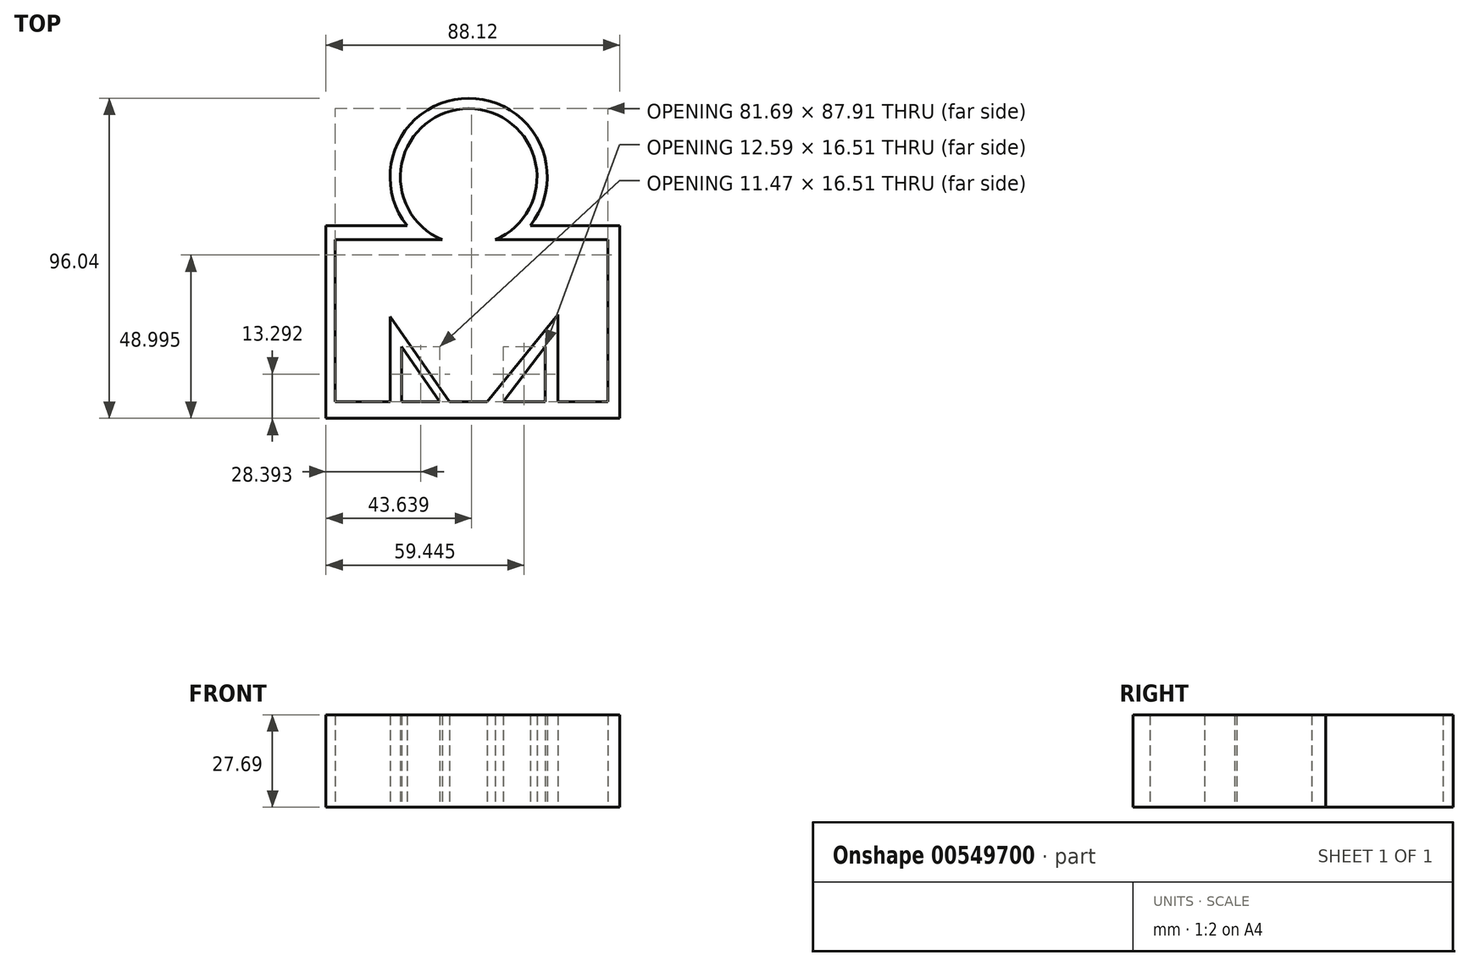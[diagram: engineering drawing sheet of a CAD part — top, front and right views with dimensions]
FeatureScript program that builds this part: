
annotation { "Feature Type Name" : "Feature", "Feature Type Description" : "" }
export const myFeature = defineFeature(function(context is Context, id is Id, definition is map)
    precondition{}
    {
        {
            var Q0;
            Q0=qCreatedBy(makeId("Top.planeOp"),FACE);
            var sketch = newSketch(context, id + "F0", { "sketchPlane" : qUnion([Q0])});
            skCircle(sketch, "E0", {"center": v(0, 0) * mm, "radius": 20.5 * mm});
            skLineSegment(sketch, "E1", {"start": v(-7.98, -18.87) * mm, "end": v(-40, -18.87) * mm});
            skLineSegment(sketch, "E2", {"start": v(-40, -18.87) * mm, "end": v(-40, -67.42) * mm});
            skLineSegment(sketch, "E3", {"start": v(-40, -67.42) * mm, "end": v(41.68, -67.42) * mm});
            skLineSegment(sketch, "E4", {"start": v(41.68, -67.42) * mm, "end": v(41.68, -18.87) * mm});
            skLineSegment(sketch, "E5", {"start": v(41.68, -18.87) * mm, "end": v(7.98, -18.87) * mm});
            skLineSegment(sketch, "E6", {"start": v(-20.14, -67.42) * mm, "end": v(-20.14, -50.92) * mm});
            skLineSegment(sketch, "E7", {"start": v(22.94, -67.42) * mm, "end": v(22.94, -50.92) * mm});
            skLineSegment(sketch, "E8", {"start": v(-20.14, -50.92) * mm, "end": v(-8.67, -67.42) * mm});
            skLineSegment(sketch, "E9", {"start": v(22.94, -50.92) * mm, "end": v(10.35, -67.42) * mm});
            skCircle(sketch, "E10", {"center": v(0, 0) * mm, "radius": 23.58 * mm});
            skLineSegment(sketch, "E11", {"start": v(-18.49, -14.64) * mm, "end": v(-42.8, -14.64) * mm});
            skLineSegment(sketch, "E12", {"start": v(-42.8, -14.64) * mm, "end": v(-42.8, -72.46) * mm});
            skLineSegment(sketch, "E13", {"start": v(-42.8, -72.46) * mm, "end": v(45.32, -72.46) * mm});
            skLineSegment(sketch, "E14", {"start": v(45.32, -72.46) * mm, "end": v(45.32, -14.64) * mm});
            skLineSegment(sketch, "E15", {"start": v(45.32, -14.64) * mm, "end": v(18.49, -14.64) * mm});
            skLineSegment(sketch, "E16", {"start": v(-23.5, -72.46) * mm, "end": v(-23.5, -41.96) * mm});
            skLineSegment(sketch, "E17", {"start": v(-23.5, -41.96) * mm, "end": v(-5.8, -67.42) * mm});
            skLineSegment(sketch, "E18", {"start": v(-5.8, -67.42) * mm, "end": v(-2.3, -72.46) * mm});
            skLineSegment(sketch, "E19", {"start": v(-2.3, -72.46) * mm, "end": v(5.32, -72.46) * mm});
            skLineSegment(sketch, "E20", {"start": v(5.32, -72.46) * mm, "end": v(1.5, -72.46) * mm});
            skLineSegment(sketch, "E21", {"start": v(1.5, -72.46) * mm, "end": v(24.62, -43.92) * mm});
            skLineSegment(sketch, "E22", {"start": v(24.62, -43.92) * mm, "end": v(26.76, -41.27) * mm});
            skLineSegment(sketch, "E23", {"start": v(26.76, -41.27) * mm, "end": v(26.76, -72.46) * mm});
            skSolve(sketch);
        }
        {
            var Q0;
            Q0 = qSketchRegion(id + "F0", true);
            var Q1;
            {var subQ0=sQuery(id+"F0.wireOp",EDGE,"E7");Q1=makeQuery(id+"F0.imprint","IMPRINT",FACE,{"disambiguationData":[TD([[makeQuery(id+"F0.imprint","IMPRINT",EDGE,{"derivedFrom":subQ0}),-1.0]])]});}
            var Q2;
            {var subQ3=sQuery(id+"F0.wireOp",EDGE,"E6");Q2=makeQuery(id+"F0.imprint","IMPRINT",FACE,{"disambiguationData":[TD([[makeQuery(id+"F0.imprint","IMPRINT",EDGE,{"derivedFrom":subQ3}),1.0]])]});}
            extrude(context, id + "F1", {"entities" : qUnion([Q0, Q1, Q2]), "depth" : 27.7 * mm, "offsetDistance" : 25.4 * mm});
        }
    });
